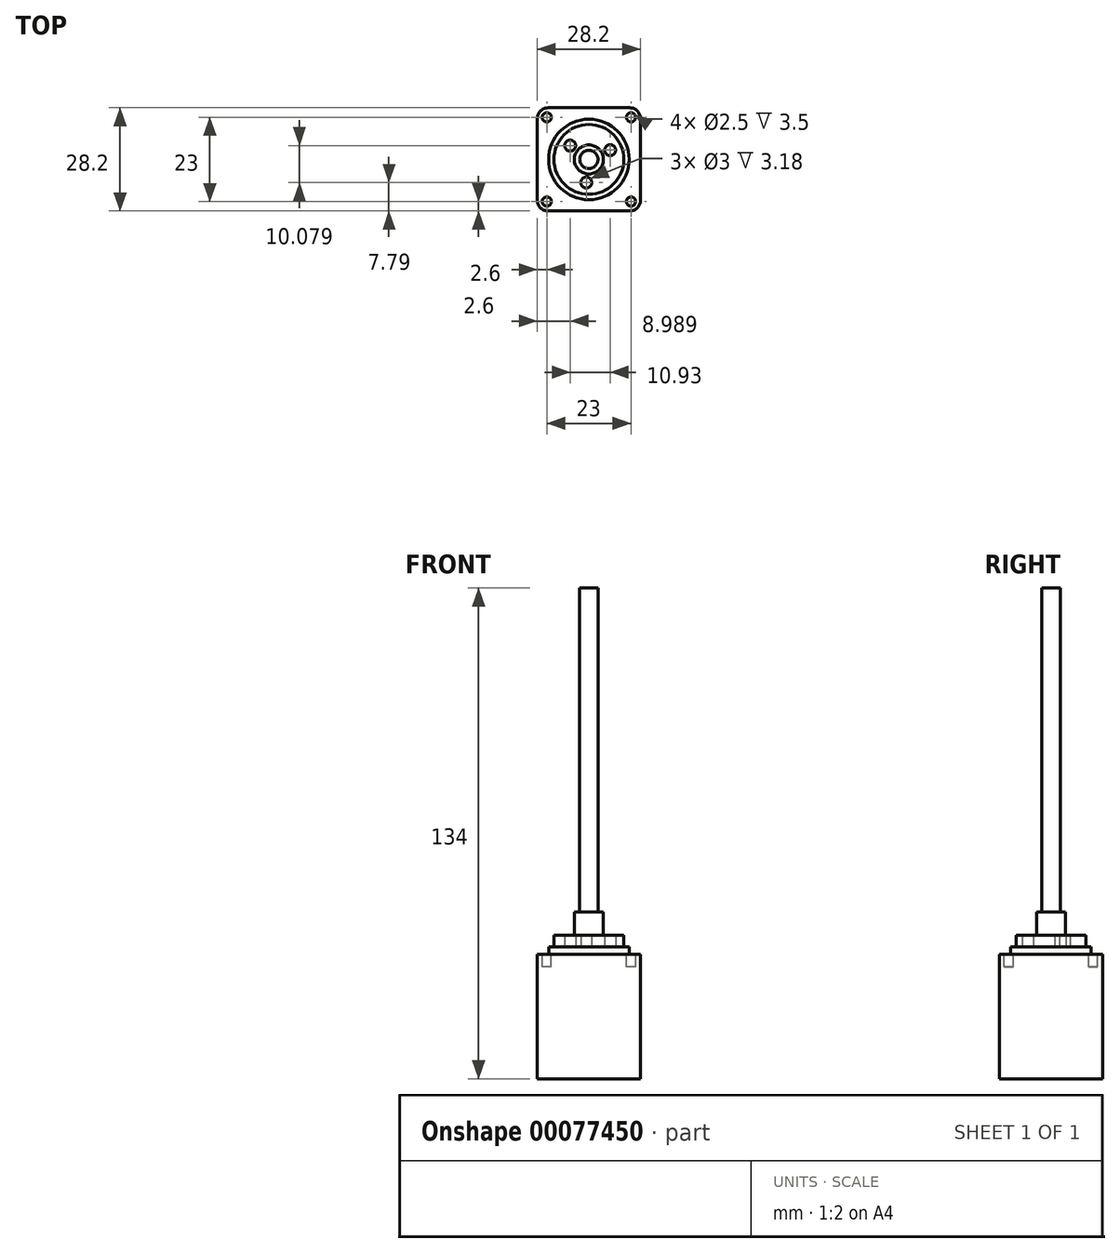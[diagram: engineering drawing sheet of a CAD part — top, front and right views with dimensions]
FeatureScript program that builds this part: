
annotation { "Feature Type Name" : "Feature", "Feature Type Description" : "" }
export const myFeature = defineFeature(function(context is Context, id is Id, definition is map)
    precondition{}
    {
        {
            var Q0;
            Q0=qCreatedBy(makeId("Front.planeOp"),FACE);
            var sketch = newSketch(context, id + "F0", { "sketchPlane" : qUnion([Q0])});
            skLineSegment(sketch, "E0.bottom", {"start": v(-14.1, 0) * mm, "end": v(14.1, 0) * mm});
            skLineSegment(sketch, "E0.top", {"start": v(-14.1, -34) * mm, "end": v(14.1, -34) * mm});
            skLineSegment(sketch, "E0.left", {"start": v(-14.1, 0) * mm, "end": v(-14.1, -34) * mm});
            skLineSegment(sketch, "E0.right", {"start": v(14.1, 0) * mm, "end": v(14.1, -34) * mm});
            skLineSegment(sketch, "E1", {"start": v(0, 54.6) * mm, "end": v(0, -51.08) * mm, "construction": true});
            skSolve(sketch);
        }
        {
            var Q0;
            Q0=makeQuery(id+"F0.imprint","IMPRINT",FACE,{"disambiguationData":[TD([[makeQuery(id+"F0.imprint","IMPRINT",EDGE,{"derivedFrom":sQuery(id+"F0.wireOp",EDGE,"E0.bottom")}),-1.0]])]});
            extrude(context, id + "F1", {"entities" : qUnion([Q0]), "endBound" : BoundingType.SYMMETRIC, "depth" : 28.2 * mm});
        }
        {
            var Q0;
            Q0=makeQuery(id+"F1.opExtrude","SWEPT_FACE",FACE,{"disambiguationData":[OSD([sQuery(id+"F0.wireOp",EDGE,"E0.bottom")])]});
            var sketch = newSketch(context, id + "F2", { "sketchPlane" : qUnion([Q0])});
            skLineSegment(sketch, "E2", {"start": v(-22.05, 0) * mm, "end": v(28.17, 0) * mm, "construction": true});
            skLineSegment(sketch, "E3", {"start": v(0, 17.29) * mm, "end": v(0, -17.48) * mm, "construction": true});
            skCircle(sketch, "E4", {"center": v(11.5, 11.5) * mm, "radius": 1.25 * mm});
            skPoint(sketch, "E5", {"position": v(0, 14.1) * mm});
            skCircle(sketch, "E6.MirrorC", {"center": v(11.5, -11.5) * mm, "radius": 1.25 * mm});
            skCircle(sketch, "E7.MirrorC", {"center": v(-11.5, -11.5) * mm, "radius": 1.25 * mm});
            skCircle(sketch, "E8.MirrorC", {"center": v(-11.5, 11.5) * mm, "radius": 1.25 * mm});
            skSolve(sketch);
        }
        {
            var Q0;
            Q0=qSketchRegion(id+"F2",true);
            extrude(context, id + "F3", {"entities" : qUnion([Q0]), "operationType" : NewBodyOperationType.REMOVE, "oppositeDirection" : true, "depth" : 3.5 * mm});
        }
        {
            var Q0;
            Q0=makeQuery(id+"F1.opExtrude","SWEPT_FACE",FACE,{"disambiguationData":[OSD([sQuery(id+"F0.wireOp",EDGE,"E0.bottom")])]});
            var sketch = newSketch(context, id + "F4", { "sketchPlane" : qUnion([Q0])});
            skCircle(sketch, "E9", {"center": v(0, 0) * mm, "radius": 11 * mm});
            skSolve(sketch);
        }
        {
            var Q0;
            Q0=qSketchRegion(id+"F4",true);
            extrude(context, id + "F5", {"entities" : qUnion([Q0]), "operationType" : NewBodyOperationType.ADD, "depth" : 2 * mm});
        }
        {
            var Q0;
            Q0=makeQuery(id+"F1.opExtrude","SWEPT_FACE",FACE,{"disambiguationData":[OSD([sQuery(id+"F0.wireOp",EDGE,"E0.bottom")])]});
            var sketch = newSketch(context, id + "F6", { "sketchPlane" : qUnion([Q0])});
            skCircle(sketch, "E10", {"center": v(0, 0) * mm, "radius": 2.5 * mm});
            skSolve(sketch);
        }
        {
            var Q0;
            Q0=qSketchRegion(id+"F6",true);
            extrude(context, id + "F7", {"entities" : qUnion([Q0]), "depth" : 100 * mm});
        }
        {
            var Q0;
            Q0=makeQuery(id+"F1.opExtrude","CAP_EDGE",EDGE,{"disambiguationData":[OSD([sQuery(id+"F0.wireOp",EDGE,"E0.left")])],"isStart":true});
            var Q1;
            Q1=makeQuery(id+"F1.opExtrude","CAP_EDGE",EDGE,{"disambiguationData":[OSD([sQuery(id+"F0.wireOp",EDGE,"E0.right")])],"isStart":true});
            var Q2;
            Q2=makeQuery(id+"F1.opExtrude","CAP_EDGE",EDGE,{"disambiguationData":[OSD([sQuery(id+"F0.wireOp",EDGE,"E0.left")])],"isStart":false});
            var Q3;
            Q3=makeQuery(id+"F1.opExtrude","CAP_EDGE",EDGE,{"disambiguationData":[OSD([sQuery(id+"F0.wireOp",EDGE,"E0.right")])],"isStart":false});
            fillet(context, id + "F8", {"entities" : qUnion([Q0, Q1, Q2, Q3]), "radius" : 3 * mm, "tangentPropagation" : true, "allowEdgeOverflow" : false});
        }
        {
            var Q0;
            Q0=makeQuery(id+"F5.opExtrude","CAP_FACE",FACE,{"disambiguationData":[OSD([sQuery(id+"F4.wireOp",EDGE,"E9")])],"isStart":false});
            var sketch = newSketch(context, id + "F9", { "sketchPlane" : qUnion([Q0])});
            skCircle(sketch, "E11", {"center": v(0, 0) * mm, "radius": 9.53 * mm});
            skCircle(sketch, "E12", {"center": v(0, 0) * mm, "radius": 2.5 * mm});
            skSolve(sketch);
        }
        {
            var Q0;
            Q0=qSketchRegion(id+"F9",true);
            extrude(context, id + "F10", {"entities" : qUnion([Q0]), "depth" : 3.18 * mm});
        }
        {
            var Q0;
            Q0=makeQuery(id+"F5.opExtrude","CAP_FACE",FACE,{"disambiguationData":[OSD([sQuery(id+"F4.wireOp",EDGE,"E9")])],"isStart":false});
            var sketch = newSketch(context, id + "F11", { "sketchPlane" : qUnion([Q0])});
            skCircle(sketch, "E13", {"center": v(0, 0) * mm, "radius": 3.97 * mm});
            skCircle(sketch, "E14", {"center": v(0, 0) * mm, "radius": 2.5 * mm});
            skSolve(sketch);
        }
        {
            var Q0;
            Q0=makeQuery(id+"F11.imprint","IMPRINT",FACE,{"disambiguationData":[TD([[makeQuery(id+"F11.imprint","IMPRINT",EDGE,{"derivedFrom":sQuery(id+"F11.wireOp",EDGE,"E13")}),1.0]])]});
            extrude(context, id + "F12", {"entities" : qUnion([Q0]), "operationType" : NewBodyOperationType.ADD, "depth" : 9.53 * mm});
        }
        {
            var Q0;
            Q0=makeQuery(id+"F5.opExtrude","CAP_FACE",FACE,{"disambiguationData":[OSD([sQuery(id+"F4.wireOp",EDGE,"E9")])],"isStart":false});
            var sketch = newSketch(context, id + "F13", { "sketchPlane" : qUnion([Q0])});
            skCircle(sketch, "E15", {"center": v(5.82, 2.54) * mm, "radius": 1.5 * mm});
            skCircle(sketch, "E16", {"center": v(0, 0) * mm, "radius": 6.35 * mm, "construction": true});
            skCircle(sketch, "E17.1.0", {"center": v(-5.11, 3.77) * mm, "radius": 1.5 * mm});
            skCircle(sketch, "E17.2.0", {"center": v(-0.7, -6.31) * mm, "radius": 1.5 * mm});
            skSolve(sketch);
        }
        {
            var Q0;
            Q0=qSketchRegion(id+"F13",true);
            extrude(context, id + "F14", {"entities" : qUnion([Q0]), "operationType" : NewBodyOperationType.REMOVE, "endBound" : BoundingType.UP_TO_NEXT, "depth" : 25 * mm});
        }
    });
